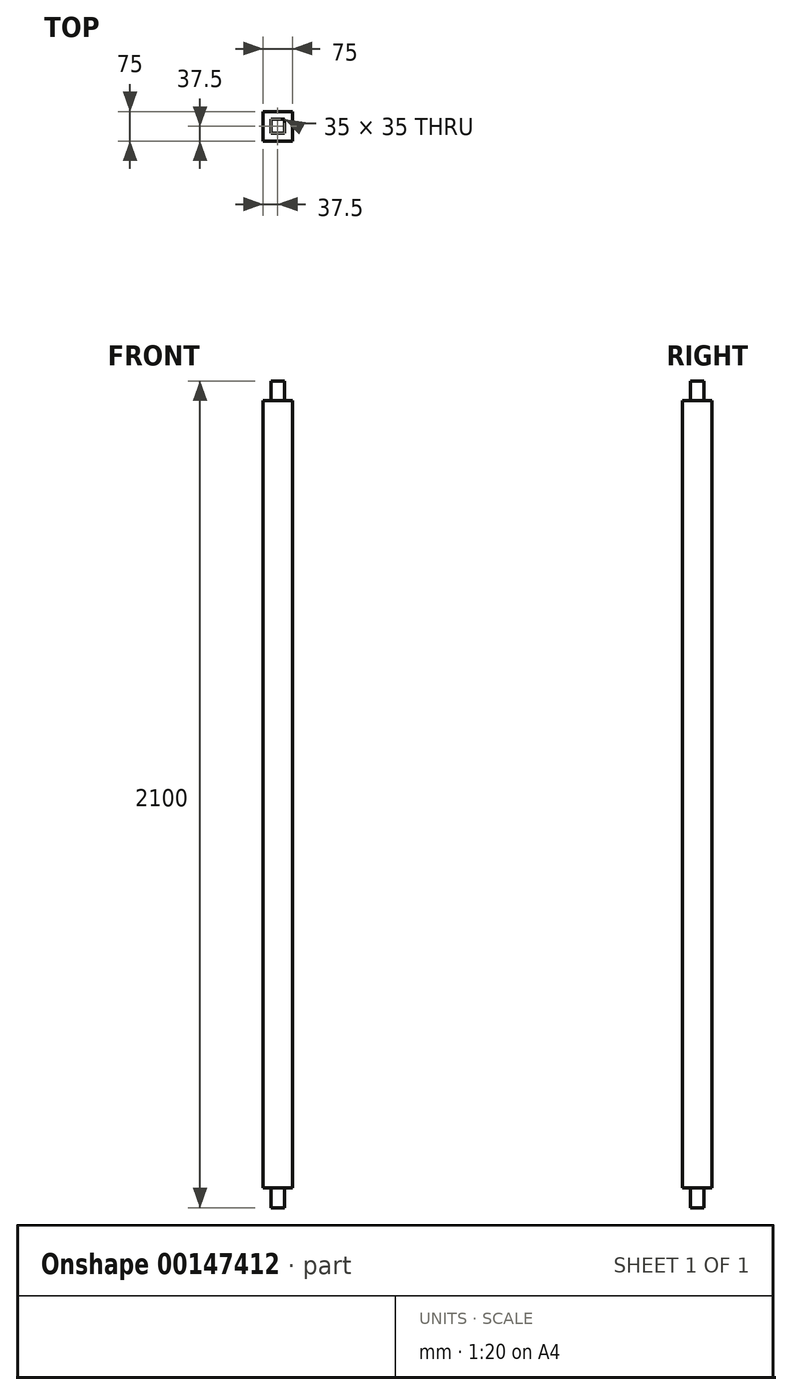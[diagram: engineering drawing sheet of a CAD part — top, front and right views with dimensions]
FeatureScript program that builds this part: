
annotation { "Feature Type Name" : "Feature", "Feature Type Description" : "" }
export const myFeature = defineFeature(function(context is Context, id is Id, definition is map)
    precondition{}
    {
        {
            var Q0;
            Q0=qCreatedBy(makeId("Top.planeOp"),FACE);
            var sketch = newSketch(context, id + "F0", { "sketchPlane" : qUnion([Q0])});
            skLineSegment(sketch, "E0.bottom", {"start": v(37.5, -37.5) * mm, "end": v(-37.5, -37.5) * mm});
            skLineSegment(sketch, "E0.top", {"start": v(37.5, 37.5) * mm, "end": v(-37.5, 37.5) * mm});
            skLineSegment(sketch, "E0.left", {"start": v(37.5, -37.5) * mm, "end": v(37.5, 37.5) * mm});
            skLineSegment(sketch, "E0.right", {"start": v(-37.5, -37.5) * mm, "end": v(-37.5, 37.5) * mm});
            skPoint(sketch, "E0.middle", {"position": v(0, 0) * mm});
            skSolve(sketch);
        }
        {
            var Q0;
            Q0=makeQuery(id+"F0.imprint","IMPRINT",FACE,{"disambiguationData":[TD([[makeQuery(id+"F0.imprint","IMPRINT",EDGE,{"derivedFrom":sQuery(id+"F0.wireOp",EDGE,"E0.bottom")}),-1.0]])]});
            extrude(context, id + "F1", {"entities" : qUnion([Q0]), "depth" : 2000 * mm});
        }
        {
            var Q0;
            Q0=makeQuery(id+"F1.opExtrude","CAP_FACE",FACE,{"disambiguationData":[OSD([sQuery(id+"F0.wireOp",EDGE,"E0.bottom"),sQuery(id+"F0.wireOp",EDGE,"E0.top"),sQuery(id+"F0.wireOp",EDGE,"E0.left"),sQuery(id+"F0.wireOp",EDGE,"E0.right")])],"isStart":false});
            var sketch = newSketch(context, id + "F2", { "sketchPlane" : qUnion([Q0])});
            skLineSegment(sketch, "E1.bottom", {"start": v(17.5, 17.5) * mm, "end": v(-17.5, 17.5) * mm});
            skLineSegment(sketch, "E1.top", {"start": v(17.5, -17.5) * mm, "end": v(-17.5, -17.5) * mm});
            skLineSegment(sketch, "E1.left", {"start": v(17.5, 17.5) * mm, "end": v(17.5, -17.5) * mm});
            skLineSegment(sketch, "E1.right", {"start": v(-17.5, 17.5) * mm, "end": v(-17.5, -17.5) * mm});
            skPoint(sketch, "E1.middle", {"position": v(0, 0) * mm});
            skSolve(sketch);
        }
        {
            var Q0;
            Q0=makeQuery(id+"F1.opExtrude","CAP_FACE",FACE,{"disambiguationData":[OSD([sQuery(id+"F0.wireOp",EDGE,"E0.bottom"),sQuery(id+"F0.wireOp",EDGE,"E0.top"),sQuery(id+"F0.wireOp",EDGE,"E0.left"),sQuery(id+"F0.wireOp",EDGE,"E0.right")])],"isStart":true});
            var sketch = newSketch(context, id + "F3", { "sketchPlane" : qUnion([Q0])});
            skLineSegment(sketch, "E2.bottom", {"start": v(17.5, -17.5) * mm, "end": v(-17.5, -17.5) * mm});
            skLineSegment(sketch, "E2.top", {"start": v(17.5, 17.5) * mm, "end": v(-17.5, 17.5) * mm});
            skLineSegment(sketch, "E2.left", {"start": v(17.5, -17.5) * mm, "end": v(17.5, 17.5) * mm});
            skLineSegment(sketch, "E2.right", {"start": v(-17.5, -17.5) * mm, "end": v(-17.5, 17.5) * mm});
            skPoint(sketch, "E2.middle", {"position": v(0, 0) * mm});
            skSolve(sketch);
        }
        {
            var Q0;
            Q0=makeQuery(id+"F2.imprint","IMPRINT",FACE,{"disambiguationData":[TD([[makeQuery(id+"F2.imprint","IMPRINT",EDGE,{"derivedFrom":sQuery(id+"F2.wireOp",EDGE,"E1.bottom")}),1.0]])]});
            extrude(context, id + "F4", {"entities" : qUnion([Q0]), "operationType" : NewBodyOperationType.ADD, "depth" : 50 * mm});
        }
        {
            var Q0;
            Q0=makeQuery(id+"F3.imprint","IMPRINT",FACE,{"disambiguationData":[TD([[makeQuery(id+"F3.imprint","IMPRINT",EDGE,{"derivedFrom":sQuery(id+"F3.wireOp",EDGE,"E2.bottom")}),-1.0]])]});
            extrude(context, id + "F5", {"entities" : qUnion([Q0]), "operationType" : NewBodyOperationType.ADD, "depth" : 50 * mm});
        }
    });
